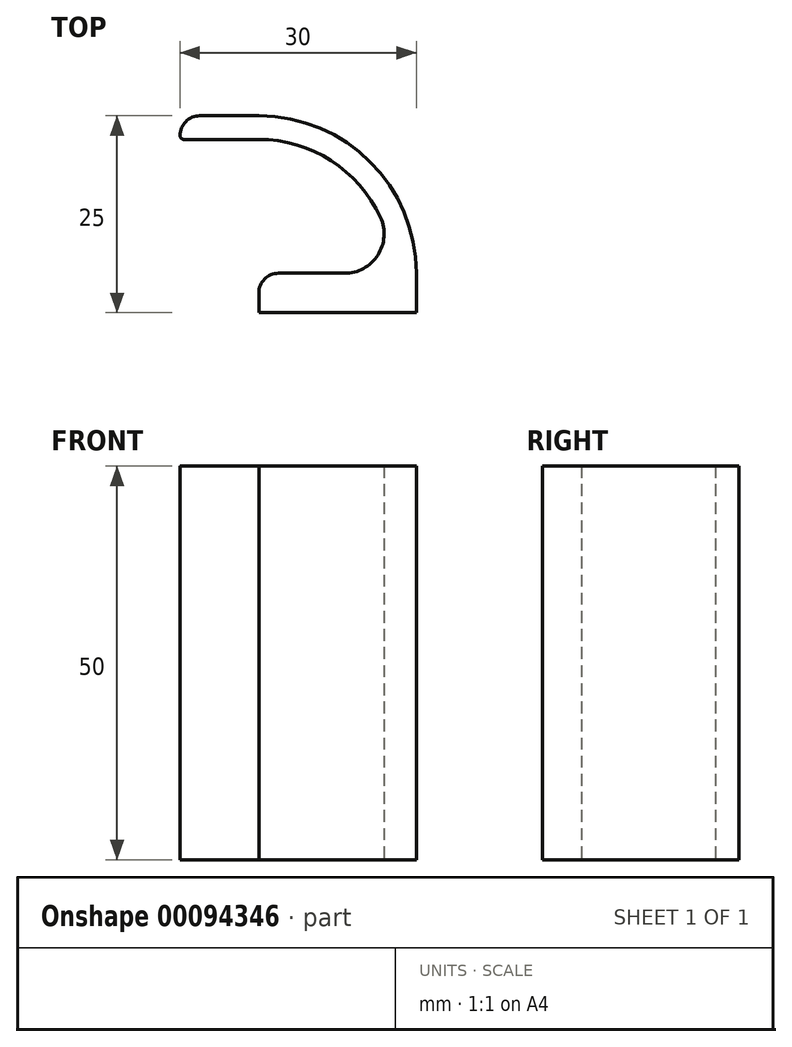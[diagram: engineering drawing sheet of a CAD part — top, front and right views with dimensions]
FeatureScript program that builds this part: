
annotation { "Feature Type Name" : "Feature", "Feature Type Description" : "" }
export const myFeature = defineFeature(function(context is Context, id is Id, definition is map)
    precondition{}
    {
        {
            var Q0;
            Q0=qCreatedBy(makeId("Top.planeOp"),FACE);
            var sketch = newSketch(context, id + "F0", { "sketchPlane" : qUnion([Q0])});
            skLineSegment(sketch, "E0.bottom", {"start": v(10, -2.5) * mm, "end": v(-10, -2.5) * mm});
            skLineSegment(sketch, "E0.top", {"start": v(10, 2.5) * mm, "end": v(-10, 2.5) * mm});
            skLineSegment(sketch, "E0.left", {"start": v(10, -2.5) * mm, "end": v(10, 2.5) * mm});
            skLineSegment(sketch, "E0.right", {"start": v(-10, -2.5) * mm, "end": v(-10, 2.5) * mm});
            skPoint(sketch, "E0.middle", {"position": v(0, 0) * mm});
            skArc(sketch, "E1", {"start": v(10, 2.5) * mm, "mid": v(4.14, 16.64) * mm, "end": v(-10, 22.5) * mm});
            skArc(sketch, "E2", {"start": v(7, 2.5) * mm, "mid": v(2.02, 14.52) * mm, "end": v(-10, 19.5) * mm});
            skLineSegment(sketch, "E3", {"start": v(-10, 22.5) * mm, "end": v(-20, 22.5) * mm});
            skLineSegment(sketch, "E4", {"start": v(-10, 19.5) * mm, "end": v(-20, 19.5) * mm});
            skLineSegment(sketch, "E5", {"start": v(-20, 22.5) * mm, "end": v(-20, 19.5) * mm});
            skSolve(sketch);
        }
        {
            var Q0;
            {var subQ1=sQuery(id+"F0.wireOp",EDGE,"E1");Q0=makeQuery(id+"F0.imprint","IMPRINT",FACE,{"disambiguationData":[TD([[makeQuery(id+"F0.imprint","IMPRINT",EDGE,{"derivedFrom":subQ1}),1.0]])]});}
            var Q1;
            Q1=makeQuery(id+"F0.imprint","IMPRINT",FACE,{"disambiguationData":[TD([[makeQuery(id+"F0.imprint","IMPRINT",EDGE,{"derivedFrom":sQuery(id+"F0.wireOp",EDGE,"E0.bottom")}),-1.0]])]});
            extrude(context, id + "F1", {"entities" : qUnion([Q0, Q1]), "depth" : 50 * mm});
        }
        {
            var Q0;
            Q0=makeQuery(id+"F1.opExtrude","SWEPT_EDGE",EDGE,{"disambiguationData":[OSD([sQuery(id+"F0.wireOp",EDGE,"E0.top"),sQuery(id+"F0.wireOp",EDGE,"E2")])]});
            fillet(context, id + "F2", {"entities" : qUnion([Q0]), "radius" : 5 * mm, "tangentPropagation" : true, "allowEdgeOverflow" : false});
        }
        {
            var Q0;
            Q0=makeQuery(id+"F1.opExtrude","SWEPT_EDGE",EDGE,{"disambiguationData":[OSD([sQuery(id+"F0.wireOp",EDGE,"E3"),sQuery(id+"F0.wireOp",EDGE,"E5")])]});
            var Q1;
            Q1=makeQuery(id+"F1.opExtrude","SWEPT_EDGE",EDGE,{"disambiguationData":[OSD([sQuery(id+"F0.wireOp",EDGE,"E0.top"),sQuery(id+"F0.wireOp",EDGE,"E0.right")])]});
            fillet(context, id + "F3", {"entities" : qUnion([Q0, Q1]), "radius" : 2.5 * mm, "tangentPropagation" : true, "allowEdgeOverflow" : false});
        }
        {
            var Q0;
            Q0=makeQuery(id+"F1.opExtrude","SWEPT_EDGE",EDGE,{"disambiguationData":[OSD([sQuery(id+"F0.wireOp",EDGE,"E4"),sQuery(id+"F0.wireOp",EDGE,"E5")])]});
            fillet(context, id + "F4", {"entities" : qUnion([Q0]), "radius" : 0.5 * mm, "tangentPropagation" : true, "allowEdgeOverflow" : false});
        }
    });
